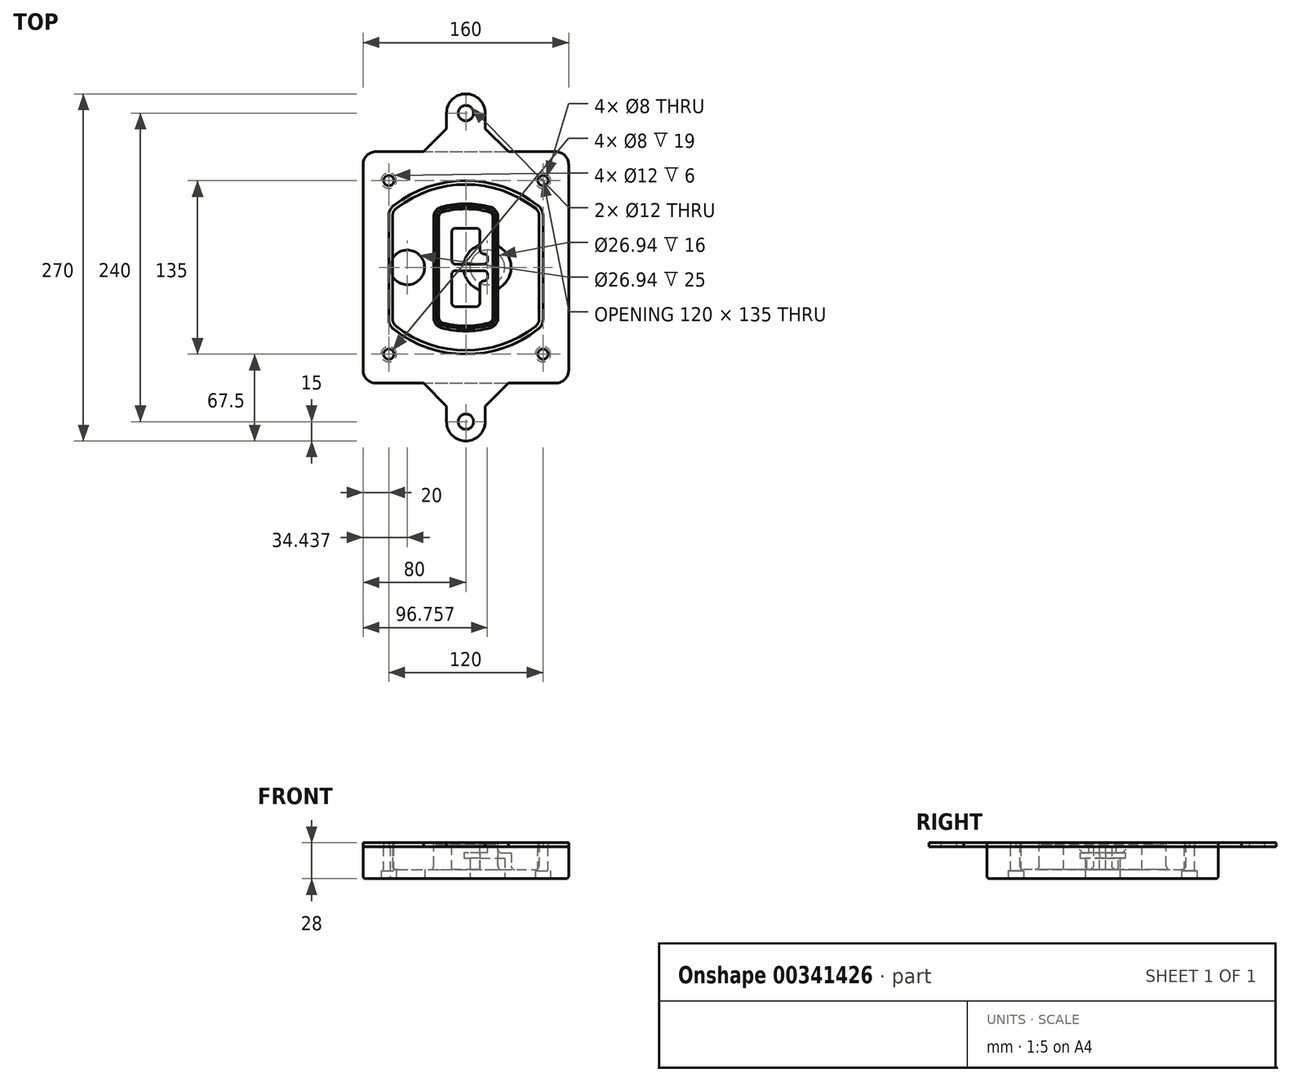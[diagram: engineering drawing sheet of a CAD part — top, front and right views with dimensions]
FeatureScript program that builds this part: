
annotation { "Feature Type Name" : "Feature", "Feature Type Description" : "" }
export const myFeature = defineFeature(function(context is Context, id is Id, definition is map)
    precondition{}
    {
        {
            var Q0;
            Q0=qCreatedBy(makeId("Top.planeOp"),FACE);
            var sketch = newSketch(context, id + "F0", { "sketchPlane" : qUnion([Q0])});
            skPoint(sketch, "E0.rect.middle", {"position": v(0, 0) * mm});
            skLineSegment(sketch, "E1.bottom", {"start": v(-70, -90) * mm, "end": v(70, -90) * mm});
            skLineSegment(sketch, "E1.top", {"start": v(-70, 90) * mm, "end": v(70, 90) * mm});
            skLineSegment(sketch, "E1.left", {"start": v(-80, -80) * mm, "end": v(-80, 80) * mm});
            skLineSegment(sketch, "E1.right", {"start": v(80, -80) * mm, "end": v(80, 80) * mm});
            skLineSegment(sketch, "E2", {"start": v(-80, 90) * mm, "end": v(80, -90) * mm, "construction": true});
            skLineSegment(sketch, "E3", {"start": v(80, 90) * mm, "end": v(-80, -90) * mm, "construction": true});
            skCircle(sketch, "E4", {"center": v(-60, 67.5) * mm, "radius": 4 * mm});
            skCircle(sketch, "E5", {"center": v(60, 67.5) * mm, "radius": 4 * mm});
            skCircle(sketch, "E6", {"center": v(60, -67.5) * mm, "radius": 4 * mm});
            skCircle(sketch, "E7", {"center": v(-60, -67.5) * mm, "radius": 4 * mm});
            skLineSegment(sketch, "E8", {"start": v(-60, 67.5) * mm, "end": v(60, 67.5) * mm, "construction": true});
            skLineSegment(sketch, "E9", {"start": v(60, 67.5) * mm, "end": v(60, -67.5) * mm, "construction": true});
            skLineSegment(sketch, "E10", {"start": v(60, -67.5) * mm, "end": v(-60, -67.5) * mm, "construction": true});
            skLineSegment(sketch, "E11", {"start": v(-60, -67.5) * mm, "end": v(-60, 67.5) * mm, "construction": true});
            skLineSegment(sketch, "E12", {"start": v(-60, 40.3) * mm, "end": v(-60, -40.3) * mm});
            skLineSegment(sketch, "E13", {"start": v(60, 40.3) * mm, "end": v(60, -40.3) * mm});
            skArc(sketch, "E14", {"start": v(56.15, 48.18) * mm, "mid": v(0, 67.5) * mm, "end": v(-56.15, 48.18) * mm});
            skArc(sketch, "E15", {"start": v(-56.15, -48.18) * mm, "mid": v(0, -67.5) * mm, "end": v(56.15, -48.18) * mm});
            skLineSegment(sketch, "E16", {"start": v(-60, 0) * mm, "end": v(60, 0) * mm, "construction": true});
            skPoint(sketch, "E17.visualSharp", {"position": v(-60, -45) * mm});
            skArc(sketch, "E17.filletArc", {"start": v(-60, -40.3) * mm, "mid": v(-58.99, -44.68) * mm, "end": v(-56.15, -48.18) * mm});
            skPoint(sketch, "E18.visualSharp", {"position": v(-60, 45) * mm});
            skArc(sketch, "E18.filletArc", {"start": v(-56.15, 48.18) * mm, "mid": v(-58.99, 44.68) * mm, "end": v(-60, 40.3) * mm});
            skPoint(sketch, "E19.visualSharp", {"position": v(60, 45) * mm});
            skArc(sketch, "E19.filletArc", {"start": v(60, 40.3) * mm, "mid": v(58.99, 44.68) * mm, "end": v(56.15, 48.18) * mm});
            skPoint(sketch, "E20.visualSharp", {"position": v(60, -45) * mm});
            skArc(sketch, "E20.filletArc", {"start": v(56.15, -48.18) * mm, "mid": v(58.99, -44.68) * mm, "end": v(60, -40.3) * mm});
            skPoint(sketch, "E21.visualSharp", {"position": v(-80, 90) * mm});
            skArc(sketch, "E21.filletArc", {"start": v(-70, 90) * mm, "mid": v(-77.07, 87.07) * mm, "end": v(-80, 80) * mm});
            skPoint(sketch, "E22.visualSharp", {"position": v(80, 90) * mm});
            skArc(sketch, "E22.filletArc", {"start": v(80, 80) * mm, "mid": v(77.07, 87.07) * mm, "end": v(70, 90) * mm});
            skPoint(sketch, "E23.visualSharp", {"position": v(80, -90) * mm});
            skArc(sketch, "E23.filletArc", {"start": v(70, -90) * mm, "mid": v(77.07, -87.07) * mm, "end": v(80, -80) * mm});
            skPoint(sketch, "E24.visualSharp", {"position": v(-80, -90) * mm});
            skArc(sketch, "E24.filletArc", {"start": v(-80, -80) * mm, "mid": v(-77.07, -87.07) * mm, "end": v(-70, -90) * mm});
            skArc(sketch, "E25.0", {"start": v(57, 40.3) * mm, "mid": v(56.3, 43.36) * mm, "end": v(54.3, 45.81) * mm});
            skLineSegment(sketch, "E25.1", {"start": v(57, 40.3) * mm, "end": v(57, -40.3) * mm});
            skArc(sketch, "E25.2", {"start": v(54.3, -45.81) * mm, "mid": v(56.3, -43.36) * mm, "end": v(57, -40.3) * mm});
            skArc(sketch, "E25.3", {"start": v(-54.3, -45.81) * mm, "mid": v(0, -64.5) * mm, "end": v(54.3, -45.81) * mm});
            skArc(sketch, "E25.4", {"start": v(-57, -40.3) * mm, "mid": v(-56.3, -43.36) * mm, "end": v(-54.3, -45.81) * mm});
            skArc(sketch, "E25.5", {"start": v(54.3, 45.81) * mm, "mid": v(0, 64.5) * mm, "end": v(-54.3, 45.81) * mm});
            skLineSegment(sketch, "E25.6", {"start": v(-57, 40.3) * mm, "end": v(-57, -40.3) * mm});
            skArc(sketch, "E25.7", {"start": v(-54.3, 45.81) * mm, "mid": v(-56.3, 43.36) * mm, "end": v(-57, 40.3) * mm});
            skArc(sketch, "E26.0", {"start": v(-58.62, 51.33) * mm, "mid": v(-62.58, 46.43) * mm, "end": v(-64, 40.3) * mm});
            skArc(sketch, "E26.1", {"start": v(58.62, 51.33) * mm, "mid": v(0, 71.5) * mm, "end": v(-58.62, 51.33) * mm});
            skArc(sketch, "E26.2", {"start": v(64, 40.3) * mm, "mid": v(62.58, 46.43) * mm, "end": v(58.62, 51.33) * mm});
            skLineSegment(sketch, "E26.3", {"start": v(64, 40.3) * mm, "end": v(64, -40.3) * mm});
            skArc(sketch, "E26.4", {"start": v(58.62, -51.33) * mm, "mid": v(62.58, -46.43) * mm, "end": v(64, -40.3) * mm});
            skLineSegment(sketch, "E26.5", {"start": v(-64, 40.3) * mm, "end": v(-64, -40.3) * mm});
            skArc(sketch, "E26.6", {"start": v(-58.62, -51.33) * mm, "mid": v(0, -71.5) * mm, "end": v(58.62, -51.33) * mm});
            skArc(sketch, "E26.7", {"start": v(-64, -40.3) * mm, "mid": v(-62.58, -46.43) * mm, "end": v(-58.62, -51.33) * mm});
            skSolve(sketch);
        }
        {
            var Q0;
            Q0=makeQuery(id+"F0.imprint","IMPRINT",FACE,{"disambiguationData":[TD([[makeQuery(id+"F0.imprint","IMPRINT",EDGE,{"derivedFrom":sQuery(id+"F0.wireOp",EDGE,"E1.bottom")}),1.0]])]});
            var Q1;
            Q1=makeQuery(id+"F0.imprint","IMPRINT",FACE,{"disambiguationData":[TD([[makeQuery(id+"F0.imprint","IMPRINT",EDGE,{"derivedFrom":sQuery(id+"F0.wireOp",EDGE,"E12")}),1.0]])]});
            var Q2;
            Q2=makeQuery(id+"F0.imprint","IMPRINT",FACE,{"disambiguationData":[TD([[makeQuery(id+"F0.imprint","IMPRINT",EDGE,{"derivedFrom":sQuery(id+"F0.wireOp",EDGE,"E25.0")}),1.0]])]});
            var Q3;
            Q3=makeQuery(id+"F0.imprint","IMPRINT",FACE,{"disambiguationData":[TD([[makeQuery(id+"F0.imprint","IMPRINT",EDGE,{"derivedFrom":sQuery(id+"F0.wireOp",EDGE,"E12")}),-1.0]])]});
            extrude(context, id + "F1", {"entities" : qUnion([Q0, Q1, Q2, Q3]), "oppositeDirection" : true, "depth" : 25 * mm});
        }
        {
            var Q0;
            Q0=makeQuery(id+"F0.imprint","IMPRINT",FACE,{"disambiguationData":[TD([[makeQuery(id+"F0.imprint","IMPRINT",EDGE,{"derivedFrom":sQuery(id+"F0.wireOp",EDGE,"E12")}),1.0]])]});
            extrude(context, id + "F2", {"entities" : qUnion([Q0]), "operationType" : NewBodyOperationType.ADD, "depth" : 3 * mm});
        }
        {
            var Q0;
            Q0=makeQuery(id+"F0.imprint","IMPRINT",FACE,{"disambiguationData":[TD([[makeQuery(id+"F0.imprint","IMPRINT",EDGE,{"derivedFrom":sQuery(id+"F0.wireOp",EDGE,"E25.0")}),1.0]])]});
            extrude(context, id + "F3", {"entities" : qUnion([Q0]), "operationType" : NewBodyOperationType.REMOVE, "oppositeDirection" : true, "depth" : 18 * mm});
        }
        {
            var Q0;
            Q0=makeQuery(id+"F2.opExtrude","CAP_FACE",FACE,{"disambiguationData":[OSD([sQuery(id+"F0.wireOp",EDGE,"E12"),sQuery(id+"F0.wireOp",EDGE,"E13"),sQuery(id+"F0.wireOp",EDGE,"E14"),sQuery(id+"F0.wireOp",EDGE,"E15"),sQuery(id+"F0.wireOp",EDGE,"E17.filletArc"),sQuery(id+"F0.wireOp",EDGE,"E18.filletArc"),sQuery(id+"F0.wireOp",EDGE,"E19.filletArc"),sQuery(id+"F0.wireOp",EDGE,"E20.filletArc"),sQuery(id+"F0.wireOp",EDGE,"E25.0"),sQuery(id+"F0.wireOp",EDGE,"E25.1"),sQuery(id+"F0.wireOp",EDGE,"E25.2"),sQuery(id+"F0.wireOp",EDGE,"E25.3"),sQuery(id+"F0.wireOp",EDGE,"E25.4"),sQuery(id+"F0.wireOp",EDGE,"E25.5"),sQuery(id+"F0.wireOp",EDGE,"E25.6"),sQuery(id+"F0.wireOp",EDGE,"E25.7")])],"isStart":false});
            var sketch = newSketch(context, id + "F4", { "sketchPlane" : qUnion([Q0])});
            skArc(sketch, "E27.0", {"start": v(-19.08, -46.97) * mm, "mid": v(0, -49.5) * mm, "end": v(19.08, -46.97) * mm});
            skArc(sketch, "E28.0", {"start": v(19.08, 46.97) * mm, "mid": v(0, 49.5) * mm, "end": v(-19.08, 46.97) * mm});
            skLineSegment(sketch, "E29", {"start": v(-25, 39.25) * mm, "end": v(-25, -39.25) * mm});
            skLineSegment(sketch, "E30", {"start": v(25, 39.25) * mm, "end": v(25, -39.25) * mm});
            skLineSegment(sketch, "E31", {"start": v(-25, 45.1) * mm, "end": v(25, 45.1) * mm, "construction": true});
            skLineSegment(sketch, "E32", {"start": v(-25, -45.1) * mm, "end": v(25, -45.1) * mm, "construction": true});
            skPoint(sketch, "E33.visualSharp", {"position": v(-25, 45.1) * mm});
            skArc(sketch, "E33.filletArc", {"start": v(-19.08, 46.97) * mm, "mid": v(-23.35, 44.11) * mm, "end": v(-25, 39.25) * mm});
            skPoint(sketch, "E34.visualSharp", {"position": v(25, 45.1) * mm});
            skArc(sketch, "E34.filletArc", {"start": v(25, 39.25) * mm, "mid": v(23.35, 44.11) * mm, "end": v(19.08, 46.97) * mm});
            skPoint(sketch, "E35.visualSharp", {"position": v(25, -45.1) * mm});
            skArc(sketch, "E35.filletArc", {"start": v(19.08, -46.97) * mm, "mid": v(23.35, -44.11) * mm, "end": v(25, -39.25) * mm});
            skPoint(sketch, "E36.visualSharp", {"position": v(-25, -45.1) * mm});
            skArc(sketch, "E36.filletArc", {"start": v(-25, -39.25) * mm, "mid": v(-23.35, -44.11) * mm, "end": v(-19.08, -46.97) * mm});
            skArc(sketch, "E37.0", {"start": v(54.3, 45.81) * mm, "mid": v(0, 64.5) * mm, "end": v(-54.3, 45.81) * mm});
            skArc(sketch, "E37.1", {"start": v(-54.3, 45.81) * mm, "mid": v(-56.3, 43.36) * mm, "end": v(-57, 40.3) * mm});
            skLineSegment(sketch, "E37.2", {"start": v(-57, 40.3) * mm, "end": v(-57, -40.3) * mm});
            skArc(sketch, "E37.3", {"start": v(-57, -40.3) * mm, "mid": v(-56.3, -43.36) * mm, "end": v(-54.3, -45.81) * mm});
            skArc(sketch, "E37.4", {"start": v(-54.3, -45.81) * mm, "mid": v(0, -64.5) * mm, "end": v(54.3, -45.81) * mm});
            skArc(sketch, "E37.5", {"start": v(54.3, -45.81) * mm, "mid": v(56.3, -43.36) * mm, "end": v(57, -40.3) * mm});
            skLineSegment(sketch, "E37.6", {"start": v(57, 40.3) * mm, "end": v(57, -40.3) * mm});
            skArc(sketch, "E37.7", {"start": v(57, 40.3) * mm, "mid": v(56.3, 43.36) * mm, "end": v(54.3, 45.81) * mm});
            skLineSegment(sketch, "E38.0", {"start": v(23, 39.25) * mm, "end": v(23, -39.25) * mm});
            skArc(sketch, "E38.1", {"start": v(18.56, -45.04) * mm, "mid": v(21.76, -42.9) * mm, "end": v(23, -39.25) * mm});
            skArc(sketch, "E38.2", {"start": v(-18.56, -45.04) * mm, "mid": v(0, -47.5) * mm, "end": v(18.56, -45.04) * mm});
            skArc(sketch, "E38.3", {"start": v(-23, -39.25) * mm, "mid": v(-21.76, -42.9) * mm, "end": v(-18.56, -45.04) * mm});
            skLineSegment(sketch, "E38.4", {"start": v(-23, 39.25) * mm, "end": v(-23, -39.25) * mm});
            skArc(sketch, "E38.5", {"start": v(23, 39.25) * mm, "mid": v(21.76, 42.9) * mm, "end": v(18.56, 45.04) * mm});
            skArc(sketch, "E38.6", {"start": v(-18.56, 45.04) * mm, "mid": v(-21.76, 42.9) * mm, "end": v(-23, 39.25) * mm});
            skArc(sketch, "E38.7", {"start": v(18.56, 45.04) * mm, "mid": v(0, 47.5) * mm, "end": v(-18.56, 45.04) * mm});
            skArc(sketch, "E39.0", {"start": v(21, 39.25) * mm, "mid": v(20.18, 41.68) * mm, "end": v(18.04, 43.1) * mm});
            skLineSegment(sketch, "E39.1", {"start": v(21, 39.25) * mm, "end": v(21, -39.25) * mm});
            skArc(sketch, "E39.2", {"start": v(18.04, -43.1) * mm, "mid": v(20.18, -41.68) * mm, "end": v(21, -39.25) * mm});
            skArc(sketch, "E39.3", {"start": v(-18.04, -43.1) * mm, "mid": v(0, -45.5) * mm, "end": v(18.04, -43.1) * mm});
            skArc(sketch, "E39.4", {"start": v(-21, -39.25) * mm, "mid": v(-20.18, -41.68) * mm, "end": v(-18.04, -43.1) * mm});
            skArc(sketch, "E39.5", {"start": v(18.04, 43.1) * mm, "mid": v(0, 45.5) * mm, "end": v(-18.04, 43.1) * mm});
            skLineSegment(sketch, "E39.6", {"start": v(-21, 39.25) * mm, "end": v(-21, -39.25) * mm});
            skArc(sketch, "E39.7", {"start": v(-18.04, 43.1) * mm, "mid": v(-20.18, 41.68) * mm, "end": v(-21, 39.25) * mm});
            skLineSegment(sketch, "E40", {"start": v(-25, 0) * mm, "end": v(25, 0) * mm, "construction": true});
            skLineSegment(sketch, "E41", {"start": v(-11, 5.5) * mm, "end": v(-11, 27.5) * mm});
            skLineSegment(sketch, "E42", {"start": v(-8, 30.5) * mm, "end": v(8, 30.5) * mm});
            skLineSegment(sketch, "E43", {"start": v(11, 27.5) * mm, "end": v(11, 13.5) * mm});
            skLineSegment(sketch, "E44", {"start": v(14, 10.5) * mm, "end": v(14, 10.5) * mm});
            skLineSegment(sketch, "E45", {"start": v(17, 7.5) * mm, "end": v(17, 5.5) * mm});
            skLineSegment(sketch, "E46", {"start": v(14, 2.5) * mm, "end": v(-8, 2.5) * mm});
            skPoint(sketch, "E47.visualSharp", {"position": v(-11, 30.5) * mm});
            skArc(sketch, "E47.filletArc", {"start": v(-8, 30.5) * mm, "mid": v(-10.12, 29.62) * mm, "end": v(-11, 27.5) * mm});
            skPoint(sketch, "E48.visualSharp", {"position": v(11, 30.5) * mm});
            skArc(sketch, "E48.filletArc", {"start": v(11, 27.5) * mm, "mid": v(10.12, 29.62) * mm, "end": v(8, 30.5) * mm});
            skPoint(sketch, "E49.visualSharp", {"position": v(11, 10.5) * mm});
            skArc(sketch, "E49.filletArc", {"start": v(11, 13.5) * mm, "mid": v(11.88, 11.38) * mm, "end": v(14, 10.5) * mm});
            skPoint(sketch, "E50.visualSharp", {"position": v(17, 10.5) * mm});
            skArc(sketch, "E50.filletArc", {"start": v(17, 7.5) * mm, "mid": v(16.12, 9.62) * mm, "end": v(14, 10.5) * mm});
            skPoint(sketch, "E51.visualSharp", {"position": v(17, 2.5) * mm});
            skArc(sketch, "E51.filletArc", {"start": v(14, 2.5) * mm, "mid": v(16.12, 3.38) * mm, "end": v(17, 5.5) * mm});
            skPoint(sketch, "E52.visualSharp", {"position": v(-11, 2.5) * mm});
            skArc(sketch, "E52.filletArc", {"start": v(-11, 5.5) * mm, "mid": v(-10.12, 3.38) * mm, "end": v(-8, 2.5) * mm});
            skLineSegment(sketch, "E53.0.MirrorCS", {"start": v(14, -2.5) * mm, "end": v(-8, -2.5) * mm});
            skArc(sketch, "E54.0.MirrorCS", {"start": v(-11, -5.5) * mm, "mid": v(-10.12, -3.38) * mm, "end": v(-8, -2.5) * mm});
            skLineSegment(sketch, "E55.0.MirrorCS", {"start": v(-11, -5.5) * mm, "end": v(-11, -27.5) * mm});
            skArc(sketch, "E56.0.MirrorCS", {"start": v(-8, -30.5) * mm, "mid": v(-10.12, -29.62) * mm, "end": v(-11, -27.5) * mm});
            skLineSegment(sketch, "E57.0.MirrorCS", {"start": v(-8, -30.5) * mm, "end": v(8, -30.5) * mm});
            skArc(sketch, "E58.0.MirrorCS", {"start": v(11, -27.5) * mm, "mid": v(10.12, -29.62) * mm, "end": v(8, -30.5) * mm});
            skLineSegment(sketch, "E59.0.MirrorCS", {"start": v(11, -27.5) * mm, "end": v(11, -13.5) * mm});
            skArc(sketch, "E60.0.MirrorCS", {"start": v(11, -13.5) * mm, "mid": v(11.88, -11.38) * mm, "end": v(14, -10.5) * mm});
            skArc(sketch, "E61.0.MirrorCS", {"start": v(17, -7.5) * mm, "mid": v(16.12, -9.62) * mm, "end": v(14, -10.5) * mm});
            skLineSegment(sketch, "E62.0.MirrorCS", {"start": v(17, -7.5) * mm, "end": v(17, -5.5) * mm});
            skArc(sketch, "E63.0.MirrorCS", {"start": v(14, -2.5) * mm, "mid": v(16.12, -3.38) * mm, "end": v(17, -5.5) * mm});
            skSolve(sketch);
        }
        {
            var Q0;
            Q0=makeQuery(id+"F4.imprint","IMPRINT",FACE,{"disambiguationData":[TD([[makeQuery(id+"F4.imprint","IMPRINT",EDGE,{"derivedFrom":sQuery(id+"F4.wireOp",EDGE,"E27.0")}),1.0]])]});
            var Q1;
            Q1=makeQuery(id+"F4.imprint","IMPRINT",FACE,{"disambiguationData":[TD([[makeQuery(id+"F4.imprint","IMPRINT",EDGE,{"derivedFrom":sQuery(id+"F4.wireOp",EDGE,"E38.0")}),-1.0]])]});
            var Q2;
            Q2=makeQuery(id+"F4.imprint","IMPRINT",FACE,{"disambiguationData":[TD([[makeQuery(id+"F4.imprint","IMPRINT",EDGE,{"derivedFrom":sQuery(id+"F4.wireOp",EDGE,"E39.0")}),1.0]])]});
            extrude(context, id + "F5", {"entities" : qUnion([Q0, Q1, Q2]), "operationType" : NewBodyOperationType.ADD, "endBound" : BoundingType.UP_TO_NEXT, "oppositeDirection" : true, "depth" : 25 * mm});
        }
        {
            var Q0;
            Q0=makeQuery(id+"F4.imprint","IMPRINT",FACE,{"disambiguationData":[TD([[makeQuery(id+"F4.imprint","IMPRINT",EDGE,{"derivedFrom":sQuery(id+"F4.wireOp",EDGE,"E38.0")}),-1.0]])]});
            extrude(context, id + "F6", {"entities" : qUnion([Q0]), "operationType" : NewBodyOperationType.REMOVE, "oppositeDirection" : true, "depth" : 2 * mm});
        }
        {
            var Q0;
            Q0=makeQuery(id+"F1.opExtrude","CAP_FACE",FACE,{"disambiguationData":[OSD([sQuery(id+"F0.wireOp",EDGE,"E1.bottom"),sQuery(id+"F0.wireOp",EDGE,"E1.top"),sQuery(id+"F0.wireOp",EDGE,"E1.left"),sQuery(id+"F0.wireOp",EDGE,"E1.right"),sQuery(id+"F0.wireOp",EDGE,"E4"),sQuery(id+"F0.wireOp",EDGE,"E5"),sQuery(id+"F0.wireOp",EDGE,"E6"),sQuery(id+"F0.wireOp",EDGE,"E7"),sQuery(id+"F0.wireOp",EDGE,"E21.filletArc"),sQuery(id+"F0.wireOp",EDGE,"E22.filletArc"),sQuery(id+"F0.wireOp",EDGE,"E23.filletArc"),sQuery(id+"F0.wireOp",EDGE,"E24.filletArc")])],"isStart":false});
            var sketch = newSketch(context, id + "F7", { "sketchPlane" : qUnion([Q0])});
            skCircle(sketch, "E64", {"center": v(16.76, 0) * mm, "radius": 13.47 * mm});
            skCircle(sketch, "E65", {"center": v(-45.56, 0) * mm, "radius": 13.47 * mm});
            skLineSegment(sketch, "E66", {"start": v(80, 0) * mm, "end": v(-80, 0) * mm});
            skCircle(sketch, "E67", {"center": v(16.76, 0) * mm, "radius": 18.47 * mm});
            skCircle(sketch, "E68", {"center": v(60, -67.5) * mm, "radius": 6 * mm});
            skCircle(sketch, "E69", {"center": v(-60, -67.5) * mm, "radius": 6 * mm});
            skCircle(sketch, "E70", {"center": v(-60, 67.5) * mm, "radius": 6 * mm});
            skCircle(sketch, "E71", {"center": v(60, 67.5) * mm, "radius": 6 * mm});
            skSolve(sketch);
        }
        {
            var Q0;
            {var subQ1=sQuery(id+"F7.wireOp",EDGE,"E66");var subQ4=sQuery(id+"F7.wireOp",EDGE,"E64");var subQ6=makeQuery(id+"F7.imprint","INTERSECT",VERTEX,{"disambiguationData":[OD(0.0)],"derivedFrom":[subQ4,subQ1]});Q0=makeQuery(id+"F7.imprint","IMPRINT",FACE,{"disambiguationData":[TD([[makeQuery(id+"F7.imprint","IMPRINT",EDGE,{"disambiguationData":[TD([[subQ6,-1.0]])],"derivedFrom":subQ4}),-1.0]])]});}
            var Q1;
            {var subQ0=sQuery(id+"F7.wireOp",EDGE,"E66");var subQ1=sQuery(id+"F7.wireOp",EDGE,"E64");var subQ3=makeQuery(id+"F7.imprint","INTERSECT",VERTEX,{"disambiguationData":[OD(0.0)],"derivedFrom":[subQ1,subQ0]});Q1=makeQuery(id+"F7.imprint","IMPRINT",FACE,{"disambiguationData":[TD([[makeQuery(id+"F7.imprint","IMPRINT",EDGE,{"disambiguationData":[TD([[subQ3,-1.0]])],"derivedFrom":subQ1}),1.0]])]});}
            var Q2;
            {var subQ0=sQuery(id+"F7.wireOp",EDGE,"E66");var subQ1=sQuery(id+"F7.wireOp",EDGE,"E64");var subQ3=makeQuery(id+"F7.imprint","INTERSECT",VERTEX,{"disambiguationData":[OD(0.0)],"derivedFrom":[subQ1,subQ0]});Q2=makeQuery(id+"F7.imprint","IMPRINT",FACE,{"disambiguationData":[TD([[makeQuery(id+"F7.imprint","IMPRINT",EDGE,{"disambiguationData":[TD([[subQ3,1.0]])],"derivedFrom":subQ1}),1.0]])]});}
            var Q3;
            {var subQ1=sQuery(id+"F7.wireOp",EDGE,"E66");var subQ4=sQuery(id+"F7.wireOp",EDGE,"E64");var subQ6=makeQuery(id+"F7.imprint","INTERSECT",VERTEX,{"disambiguationData":[OD(0.0)],"derivedFrom":[subQ4,subQ1]});Q3=makeQuery(id+"F7.imprint","IMPRINT",FACE,{"disambiguationData":[TD([[makeQuery(id+"F7.imprint","IMPRINT",EDGE,{"disambiguationData":[TD([[subQ6,1.0]])],"derivedFrom":subQ4}),-1.0]])]});}
            extrude(context, id + "F8", {"entities" : qUnion([Q0, Q1, Q2, Q3]), "operationType" : NewBodyOperationType.ADD, "oppositeDirection" : true, "depth" : 20 * mm});
        }
        {
            var Q0;
            {var subQ0=sQuery(id+"F7.wireOp",EDGE,"E66");var subQ1=sQuery(id+"F7.wireOp",EDGE,"E64");var subQ3=makeQuery(id+"F7.imprint","INTERSECT",VERTEX,{"disambiguationData":[OD(0.0)],"derivedFrom":[subQ1,subQ0]});Q0=makeQuery(id+"F7.imprint","IMPRINT",FACE,{"disambiguationData":[TD([[makeQuery(id+"F7.imprint","IMPRINT",EDGE,{"disambiguationData":[TD([[subQ3,-1.0]])],"derivedFrom":subQ1}),1.0]])]});}
            var Q1;
            {var subQ0=sQuery(id+"F7.wireOp",EDGE,"E66");var subQ1=sQuery(id+"F7.wireOp",EDGE,"E64");var subQ3=makeQuery(id+"F7.imprint","INTERSECT",VERTEX,{"disambiguationData":[OD(0.0)],"derivedFrom":[subQ1,subQ0]});Q1=makeQuery(id+"F7.imprint","IMPRINT",FACE,{"disambiguationData":[TD([[makeQuery(id+"F7.imprint","IMPRINT",EDGE,{"disambiguationData":[TD([[subQ3,1.0]])],"derivedFrom":subQ1}),1.0]])]});}
            extrude(context, id + "F9", {"entities" : qUnion([Q0, Q1]), "operationType" : NewBodyOperationType.REMOVE, "oppositeDirection" : true, "depth" : 16 * mm});
        }
        {
            var Q0;
            {var subQ0=sQuery(id+"F7.wireOp",EDGE,"E66");var subQ1=sQuery(id+"F7.wireOp",EDGE,"E65");var subQ3=makeQuery(id+"F7.imprint","INTERSECT",VERTEX,{"disambiguationData":[OD(0.0)],"derivedFrom":[subQ1,subQ0]});Q0=makeQuery(id+"F7.imprint","IMPRINT",FACE,{"disambiguationData":[TD([[makeQuery(id+"F7.imprint","IMPRINT",EDGE,{"disambiguationData":[TD([[subQ3,-1.0]])],"derivedFrom":subQ1}),1.0]])]});}
            var Q1;
            {var subQ0=sQuery(id+"F7.wireOp",EDGE,"E66");var subQ1=sQuery(id+"F7.wireOp",EDGE,"E65");var subQ3=makeQuery(id+"F7.imprint","INTERSECT",VERTEX,{"disambiguationData":[OD(0.0)],"derivedFrom":[subQ1,subQ0]});Q1=makeQuery(id+"F7.imprint","IMPRINT",FACE,{"disambiguationData":[TD([[makeQuery(id+"F7.imprint","IMPRINT",EDGE,{"disambiguationData":[TD([[subQ3,1.0]])],"derivedFrom":subQ1}),1.0]])]});}
            extrude(context, id + "F10", {"entities" : qUnion([Q0, Q1]), "operationType" : NewBodyOperationType.REMOVE, "oppositeDirection" : true, "depth" : 25 * mm});
        }
        {
            var Q0;
            Q0=makeQuery(id+"F7.imprint","IMPRINT",FACE,{"disambiguationData":[TD([[makeQuery(id+"F7.imprint","IMPRINT",EDGE,{"derivedFrom":sQuery(id+"F7.wireOp",EDGE,"E68")}),1.0]])]});
            var Q1;
            Q1=makeQuery(id+"F7.imprint","IMPRINT",FACE,{"disambiguationData":[TD([[makeQuery(id+"F7.imprint","IMPRINT",EDGE,{"derivedFrom":makeQuery(id+"F1.opExtrude","CAP_EDGE",EDGE,{"disambiguationData":[OSD([sQuery(id+"F0.wireOp",EDGE,"E5")])],"isStart":false})}),-1.0]])]});
            var Q2;
            Q2=makeQuery(id+"F7.imprint","IMPRINT",FACE,{"disambiguationData":[TD([[makeQuery(id+"F7.imprint","IMPRINT",EDGE,{"derivedFrom":sQuery(id+"F7.wireOp",EDGE,"E69")}),1.0]])]});
            var Q3;
            Q3=makeQuery(id+"F7.imprint","IMPRINT",FACE,{"disambiguationData":[TD([[makeQuery(id+"F7.imprint","IMPRINT",EDGE,{"derivedFrom":makeQuery(id+"F1.opExtrude","CAP_EDGE",EDGE,{"disambiguationData":[OSD([sQuery(id+"F0.wireOp",EDGE,"E4")])],"isStart":false})}),-1.0]])]});
            var Q4;
            Q4=makeQuery(id+"F7.imprint","IMPRINT",FACE,{"disambiguationData":[TD([[makeQuery(id+"F7.imprint","IMPRINT",EDGE,{"derivedFrom":sQuery(id+"F7.wireOp",EDGE,"E70")}),1.0]])]});
            var Q5;
            Q5=makeQuery(id+"F7.imprint","IMPRINT",FACE,{"disambiguationData":[TD([[makeQuery(id+"F7.imprint","IMPRINT",EDGE,{"derivedFrom":makeQuery(id+"F1.opExtrude","CAP_EDGE",EDGE,{"disambiguationData":[OSD([sQuery(id+"F0.wireOp",EDGE,"E7")])],"isStart":false})}),-1.0]])]});
            var Q6;
            Q6=makeQuery(id+"F7.imprint","IMPRINT",FACE,{"disambiguationData":[TD([[makeQuery(id+"F7.imprint","IMPRINT",EDGE,{"derivedFrom":sQuery(id+"F7.wireOp",EDGE,"E71")}),1.0]])]});
            var Q7;
            Q7=makeQuery(id+"F7.imprint","IMPRINT",FACE,{"disambiguationData":[TD([[makeQuery(id+"F7.imprint","IMPRINT",EDGE,{"derivedFrom":makeQuery(id+"F1.opExtrude","CAP_EDGE",EDGE,{"disambiguationData":[OSD([sQuery(id+"F0.wireOp",EDGE,"E6")])],"isStart":false})}),-1.0]])]});
            extrude(context, id + "F11", {"entities" : qUnion([Q0, Q1, Q2, Q3, Q4, Q5, Q6, Q7]), "operationType" : NewBodyOperationType.REMOVE, "oppositeDirection" : true, "depth" : 6 * mm});
        }
        {
            var Q0;
            Q0=makeQuery(id+"F9.boolean.opBoolean","COPY",FACE,{"derivedFrom":makeQuery(id+"F9.opExtrude","CAP_FACE",FACE,{"disambiguationData":[OSD([sQuery(id+"F7.wireOp",EDGE,"E64")])],"isStart":false})});
            var sketch = newSketch(context, id + "F12", { "sketchPlane" : qUnion([Q0])});
            skArc(sketch, "E72.0", {"start": v(11, 17.55) * mm, "mid": v(2.57, 11.82) * mm, "end": v(-1.54, 2.5) * mm});
            skArc(sketch, "E72.1", {"start": v(-1.54, -2.5) * mm, "mid": v(2.57, -11.82) * mm, "end": v(11, -17.55) * mm});
            skLineSegment(sketch, "E73", {"start": v(-1.54, -2.5) * mm, "end": v(14, -2.5) * mm});
            skLineSegment(sketch, "E74.0", {"start": v(14, 2.5) * mm, "end": v(-1.54, 2.5) * mm});
            skArc(sketch, "E74.1", {"start": v(14, 2.5) * mm, "mid": v(16.12, 3.38) * mm, "end": v(17, 5.5) * mm});
            skLineSegment(sketch, "E74.2", {"start": v(17, 7.5) * mm, "end": v(17, 5.5) * mm});
            skArc(sketch, "E74.3", {"start": v(17, 7.5) * mm, "mid": v(16.12, 9.62) * mm, "end": v(14, 10.5) * mm});
            skArc(sketch, "E74.4", {"start": v(11, 13.5) * mm, "mid": v(11.88, 11.38) * mm, "end": v(14, 10.5) * mm});
            skLineSegment(sketch, "E74.5", {"start": v(11, 17.55) * mm, "end": v(11, 13.5) * mm});
            skLineSegment(sketch, "E74.7", {"start": v(14, -2.5) * mm, "end": v(-1.54, -2.5) * mm});
            skArc(sketch, "E74.8", {"start": v(14, -2.5) * mm, "mid": v(16.12, -3.38) * mm, "end": v(17, -5.5) * mm});
            skLineSegment(sketch, "E74.9", {"start": v(17, -7.5) * mm, "end": v(17, -5.5) * mm});
            skArc(sketch, "E74.10", {"start": v(17, -7.5) * mm, "mid": v(16.12, -9.62) * mm, "end": v(14, -10.5) * mm});
            skArc(sketch, "E74.11", {"start": v(11, -13.5) * mm, "mid": v(11.88, -11.38) * mm, "end": v(14, -10.5) * mm});
            skLineSegment(sketch, "E74.12", {"start": v(11, -17.55) * mm, "end": v(11, -13.5) * mm});
            skPoint(sketch, "E75.orphan", {"position": v(11, -27.5) * mm});
            skPoint(sketch, "E76.orphan", {"position": v(-8, -2.5) * mm});
            skPoint(sketch, "E77.orphan", {"position": v(-8, 2.5) * mm});
            skPoint(sketch, "E78.orphan", {"position": v(11, 27.5) * mm});
            skSolve(sketch);
        }
        {
            var Q0;
            {var subQ7=sQuery(id+"F12.wireOp",EDGE,"E72.0");var subQ14=sQuery(id+"F12.wireOp",EDGE,"E72.1");var subQ16=sQuery(id+"F12.wireOp",EDGE,"E74.1");var subQ18=sQuery(id+"F12.wireOp",EDGE,"E74.8");Q0=qUnion([makeQuery(id+"F12.imprint","IMPRINT",FACE,{"disambiguationData":[TD([[makeQuery(id+"F12.imprint","IMPRINT",EDGE,{"derivedFrom":subQ7}),1.0]])]}),makeQuery(id+"F12.imprint","IMPRINT",FACE,{"disambiguationData":[TD([[makeQuery(id+"F12.imprint","IMPRINT",EDGE,{"derivedFrom":subQ14}),1.0]])]}),makeQuery(id+"F12.imprint","IMPRINT",FACE,{"disambiguationData":[TD([[makeQuery(id+"F12.imprint","IMPRINT",EDGE,{"derivedFrom":subQ16}),1.0]])]}),makeQuery(id+"F12.imprint","IMPRINT",FACE,{"disambiguationData":[TD([[makeQuery(id+"F12.imprint","IMPRINT",EDGE,{"derivedFrom":subQ18}),-1.0]])]})]);}
            var Q1;
            Q1=makeQuery(id+"F5.boolean.opBoolean","SPLIT",FACE,{"disambiguationData":[TD([makeQuery(id+"F5.opExtrude","SWEPT_FACE",FACE,{"disambiguationData":[OSD([sQuery(id+"F4.wireOp",EDGE,"E41")])]})])],"derivedFrom":makeQuery(id+"F3.boolean.opBoolean","COPY",FACE,{"derivedFrom":makeQuery(id+"F3.opExtrude","CAP_FACE",FACE,{"disambiguationData":[OSD([sQuery(id+"F0.wireOp",EDGE,"E25.0"),sQuery(id+"F0.wireOp",EDGE,"E25.1"),sQuery(id+"F0.wireOp",EDGE,"E25.2"),sQuery(id+"F0.wireOp",EDGE,"E25.3"),sQuery(id+"F0.wireOp",EDGE,"E25.4"),sQuery(id+"F0.wireOp",EDGE,"E25.5"),sQuery(id+"F0.wireOp",EDGE,"E25.6"),sQuery(id+"F0.wireOp",EDGE,"E25.7")])],"isStart":false})})});
            extrude(context, id + "F13", {"entities" : qUnion([Q0]), "operationType" : NewBodyOperationType.REMOVE, "endBound" : BoundingType.UP_TO_SURFACE, "endBoundEntityFace" : qUnion([Q1]), "depth" : 25 * mm});
        }
        {
            var Q0;
            Q0=makeQuery(id+"F3.boolean.opBoolean","COPY",EDGE,{"derivedFrom":makeQuery(id+"F3.opExtrude","CAP_EDGE",EDGE,{"disambiguationData":[OSD([sQuery(id+"F0.wireOp",EDGE,"E25.6")])],"isStart":false})});
            var Q1;
            Q1=makeQuery(id+"F8.boolean.opBoolean","INTERSECT",EDGE,{"derivedFrom":[makeQuery(id+"F5.opExtrude","SWEPT_FACE",FACE,{"disambiguationData":[OSD([sQuery(id+"F4.wireOp",EDGE,"E30")])]}),makeQuery(id+"F8.opExtrude","CAP_FACE",FACE,{"disambiguationData":[OSD([sQuery(id+"F7.wireOp",EDGE,"E67")])],"isStart":false})]});
            var Q2;
            Q2=makeQuery(id+"F8.boolean.opBoolean","INTERSECT",EDGE,{"disambiguationData":[OD(1.0)],"derivedFrom":[makeQuery(id+"F5.opExtrude","SWEPT_FACE",FACE,{"disambiguationData":[OSD([sQuery(id+"F4.wireOp",EDGE,"E30")])]}),makeQuery(id+"F8.opExtrude","SWEPT_FACE",FACE,{"disambiguationData":[OSD([sQuery(id+"F7.wireOp",EDGE,"E67")])]})]});
            var Q3;
            {var subQ0=sQuery(id+"F4.wireOp",EDGE,"E30");Q3=makeQuery(id+"F8.boolean.opBoolean","SPLIT",EDGE,{"disambiguationData":[TD([makeQuery(id+"F5.opExtrude","SWEPT_FACE",FACE,{"disambiguationData":[OSD([sQuery(id+"F4.wireOp",EDGE,"E35.filletArc")])]})])],"derivedFrom":makeQuery(id+"F5.opExtrude","CAP_EDGE",EDGE,{"disambiguationData":[OSD([subQ0])],"isStart":false})});}
            var Q4;
            {var subQ0=sQuery(id+"F0.wireOp",EDGE,"E25.7");var subQ1=sQuery(id+"F0.wireOp",EDGE,"E25.1");var subQ2=sQuery(id+"F0.wireOp",EDGE,"E25.6");var subQ3=sQuery(id+"F0.wireOp",EDGE,"E25.5");var subQ4=sQuery(id+"F0.wireOp",EDGE,"E25.4");var subQ5=sQuery(id+"F0.wireOp",EDGE,"E25.0");var subQ6=sQuery(id+"F0.wireOp",EDGE,"E25.2");var subQ7=sQuery(id+"F0.wireOp",EDGE,"E25.3");Q4=makeQuery(id+"F8.boolean.opBoolean","INTERSECT",EDGE,{"derivedFrom":[makeQuery(id+"F5.boolean.opBoolean","SPLIT",FACE,{"disambiguationData":[TD([makeQuery(id+"F2.opExtrude","SWEPT_FACE",FACE,{"disambiguationData":[OSD([subQ5])]})])],"derivedFrom":makeQuery(id+"F3.boolean.opBoolean","COPY",FACE,{"derivedFrom":makeQuery(id+"F3.opExtrude","CAP_FACE",FACE,{"disambiguationData":[OSD([subQ5,subQ1,subQ6,subQ7,subQ4,subQ3,subQ2,subQ0])],"isStart":false})})}),makeQuery(id+"F8.opExtrude","SWEPT_FACE",FACE,{"disambiguationData":[OSD([sQuery(id+"F7.wireOp",EDGE,"E67")])]})]});}
            var Q5;
            Q5=makeQuery(id+"F8.boolean.opBoolean","INTERSECT",EDGE,{"disambiguationData":[OD(0.0)],"derivedFrom":[makeQuery(id+"F5.opExtrude","SWEPT_FACE",FACE,{"disambiguationData":[OSD([sQuery(id+"F4.wireOp",EDGE,"E30")])]}),makeQuery(id+"F8.opExtrude","SWEPT_FACE",FACE,{"disambiguationData":[OSD([sQuery(id+"F7.wireOp",EDGE,"E67")])]})]});
            fillet(context, id + "F14", {"entities" : qUnion([Q0, Q1, Q2, Q3, Q4, Q5]), "radius" : 3 * mm, "tangentPropagation" : true, "allowEdgeOverflow" : false});
        }
        {
            var Q0;
            Q0=makeQuery(id+"F1.opExtrude","CAP_EDGE",EDGE,{"disambiguationData":[OSD([sQuery(id+"F0.wireOp",EDGE,"E1.bottom")])],"isStart":false});
            fillet(context, id + "F15", {"entities" : qUnion([Q0]), "radius" : 2 * mm, "tangentPropagation" : true, "allowEdgeOverflow" : false});
        }
        {
            var Q0;
            {var subQ0=sQuery(id+"F0.wireOp",EDGE,"E21.filletArc");var subQ1=sQuery(id+"F0.wireOp",EDGE,"E7");var subQ2=sQuery(id+"F0.wireOp",EDGE,"E6");var subQ3=sQuery(id+"F0.wireOp",EDGE,"E5");var subQ4=sQuery(id+"F0.wireOp",EDGE,"E4");var subQ5=sQuery(id+"F0.wireOp",EDGE,"E22.filletArc");var subQ6=sQuery(id+"F0.wireOp",EDGE,"E1.bottom");var subQ7=sQuery(id+"F0.wireOp",EDGE,"E1.right");var subQ8=sQuery(id+"F0.wireOp",EDGE,"E1.top");var subQ9=sQuery(id+"F0.wireOp",EDGE,"E1.left");var subQ10=sQuery(id+"F0.wireOp",EDGE,"E23.filletArc");var subQ11=sQuery(id+"F0.wireOp",EDGE,"E24.filletArc");Q0=makeQuery(id+"F2.boolean.opBoolean","SPLIT",FACE,{"disambiguationData":[TD([makeQuery(id+"F1.opExtrude","SWEPT_FACE",FACE,{"disambiguationData":[OSD([subQ6])]})])],"derivedFrom":makeQuery(id+"F1.opExtrude","CAP_FACE",FACE,{"disambiguationData":[OSD([subQ6,subQ8,subQ9,subQ7,subQ4,subQ3,subQ2,subQ1,subQ0,subQ5,subQ10,subQ11])],"isStart":true})});}
            var sketch = newSketch(context, id + "F16", { "sketchPlane" : qUnion([Q0])});
            skArc(sketch, "E79.0", {"start": v(56.15, 48.18) * mm, "mid": v(0, 67.5) * mm, "end": v(-56.15, 48.18) * mm});
            skLineSegment(sketch, "E79.1", {"start": v(-60, 40.3) * mm, "end": v(-60, -40.3) * mm});
            skArc(sketch, "E79.2", {"start": v(-56.15, 48.18) * mm, "mid": v(-58.99, 44.68) * mm, "end": v(-60, 40.3) * mm});
            skArc(sketch, "E79.3", {"start": v(-56.15, -48.18) * mm, "mid": v(0, -67.5) * mm, "end": v(56.15, -48.18) * mm});
            skArc(sketch, "E79.4", {"start": v(-60, -40.3) * mm, "mid": v(-58.99, -44.68) * mm, "end": v(-56.15, -48.18) * mm});
            skArc(sketch, "E79.5", {"start": v(56.15, -48.18) * mm, "mid": v(58.99, -44.68) * mm, "end": v(60, -40.3) * mm});
            skLineSegment(sketch, "E79.6", {"start": v(60, 40.3) * mm, "end": v(60, -40.3) * mm});
            skArc(sketch, "E79.7", {"start": v(60, 40.3) * mm, "mid": v(58.99, 44.68) * mm, "end": v(56.15, 48.18) * mm});
            skLineSegment(sketch, "E79.8", {"start": v(-70, 90) * mm, "end": v(70, 90) * mm});
            skArc(sketch, "E79.9", {"start": v(80, 80) * mm, "mid": v(77.07, 87.07) * mm, "end": v(70, 90) * mm});
            skLineSegment(sketch, "E79.10", {"start": v(80, -80) * mm, "end": v(80, 80) * mm});
            skArc(sketch, "E79.11", {"start": v(70, -90) * mm, "mid": v(77.07, -87.07) * mm, "end": v(80, -80) * mm});
            skLineSegment(sketch, "E79.12", {"start": v(-70, -90) * mm, "end": v(70, -90) * mm});
            skArc(sketch, "E79.13", {"start": v(-80, -80) * mm, "mid": v(-77.07, -87.07) * mm, "end": v(-70, -90) * mm});
            skLineSegment(sketch, "E79.14", {"start": v(-80, -80) * mm, "end": v(-80, 80) * mm});
            skArc(sketch, "E79.15", {"start": v(-70, 90) * mm, "mid": v(-77.07, 87.07) * mm, "end": v(-80, 80) * mm});
            skCircle(sketch, "E79.16", {"center": v(-60, 67.5) * mm, "radius": 4 * mm});
            skCircle(sketch, "E79.17", {"center": v(-60, -67.5) * mm, "radius": 4 * mm});
            skCircle(sketch, "E79.18", {"center": v(60, -67.5) * mm, "radius": 4 * mm});
            skCircle(sketch, "E79.19", {"center": v(60, 67.5) * mm, "radius": 4 * mm});
            skLineSegment(sketch, "E80", {"start": v(0, 90) * mm, "end": v(0, 120) * mm, "construction": true});
            skPoint(sketch, "E80.endSnap0", {"position": v(0, 90) * mm});
            skLineSegment(sketch, "E81", {"start": v(-33, 90) * mm, "end": v(-15, 108) * mm});
            skLineSegment(sketch, "E82", {"start": v(-15, 108) * mm, "end": v(-15, 120) * mm});
            skLineSegment(sketch, "E83", {"start": v(33, 90) * mm, "end": v(15, 108) * mm});
            skLineSegment(sketch, "E84", {"start": v(15, 108) * mm, "end": v(15, 120) * mm});
            skArc(sketch, "E85", {"start": v(15, 120) * mm, "mid": v(0, 135) * mm, "end": v(-15, 120) * mm});
            skCircle(sketch, "E86", {"center": v(0, 120) * mm, "radius": 6 * mm});
            skLineSegment(sketch, "E87", {"start": v(-80, 0) * mm, "end": v(80, 0) * mm, "construction": true});
            skLineSegment(sketch, "E88.MirrorCS", {"start": v(-33, -90) * mm, "end": v(-15, -108) * mm});
            skArc(sketch, "E89.MirrorCS", {"start": v(15, -120) * mm, "mid": v(0, -135) * mm, "end": v(-15, -120) * mm});
            skCircle(sketch, "E90.MirrorC", {"center": v(0, -120) * mm, "radius": 6 * mm});
            skLineSegment(sketch, "E91.MirrorCS", {"start": v(15, -108) * mm, "end": v(15, -120) * mm});
            skLineSegment(sketch, "E92.MirrorCS", {"start": v(33, -90) * mm, "end": v(15, -108) * mm});
            skLineSegment(sketch, "E93.MirrorCS", {"start": v(0, -90) * mm, "end": v(0, -120) * mm, "construction": true});
            skLineSegment(sketch, "E94.MirrorCS", {"start": v(-15, -108) * mm, "end": v(-15, -120) * mm});
            skSolve(sketch);
        }
        {
            var Q0;
            Q0 = qSketchRegion(id + "F16", true);
            var Q1;
            Q1=makeQuery(id+"F2.opExtrude","CAP_FACE",FACE,{"disambiguationData":[OSD([sQuery(id+"F0.wireOp",EDGE,"E12"),sQuery(id+"F0.wireOp",EDGE,"E13"),sQuery(id+"F0.wireOp",EDGE,"E14"),sQuery(id+"F0.wireOp",EDGE,"E15"),sQuery(id+"F0.wireOp",EDGE,"E17.filletArc"),sQuery(id+"F0.wireOp",EDGE,"E18.filletArc"),sQuery(id+"F0.wireOp",EDGE,"E19.filletArc"),sQuery(id+"F0.wireOp",EDGE,"E20.filletArc"),sQuery(id+"F0.wireOp",EDGE,"E25.0"),sQuery(id+"F0.wireOp",EDGE,"E25.1"),sQuery(id+"F0.wireOp",EDGE,"E25.2"),sQuery(id+"F0.wireOp",EDGE,"E25.3"),sQuery(id+"F0.wireOp",EDGE,"E25.4"),sQuery(id+"F0.wireOp",EDGE,"E25.5"),sQuery(id+"F0.wireOp",EDGE,"E25.6"),sQuery(id+"F0.wireOp",EDGE,"E25.7")])],"isStart":false});
            extrude(context, id + "F17", {"entities" : qUnion([Q0]), "endBound" : BoundingType.UP_TO_SURFACE, "endBoundEntityFace" : qUnion([Q1]), "depth" : 25 * mm});
        }
    });
